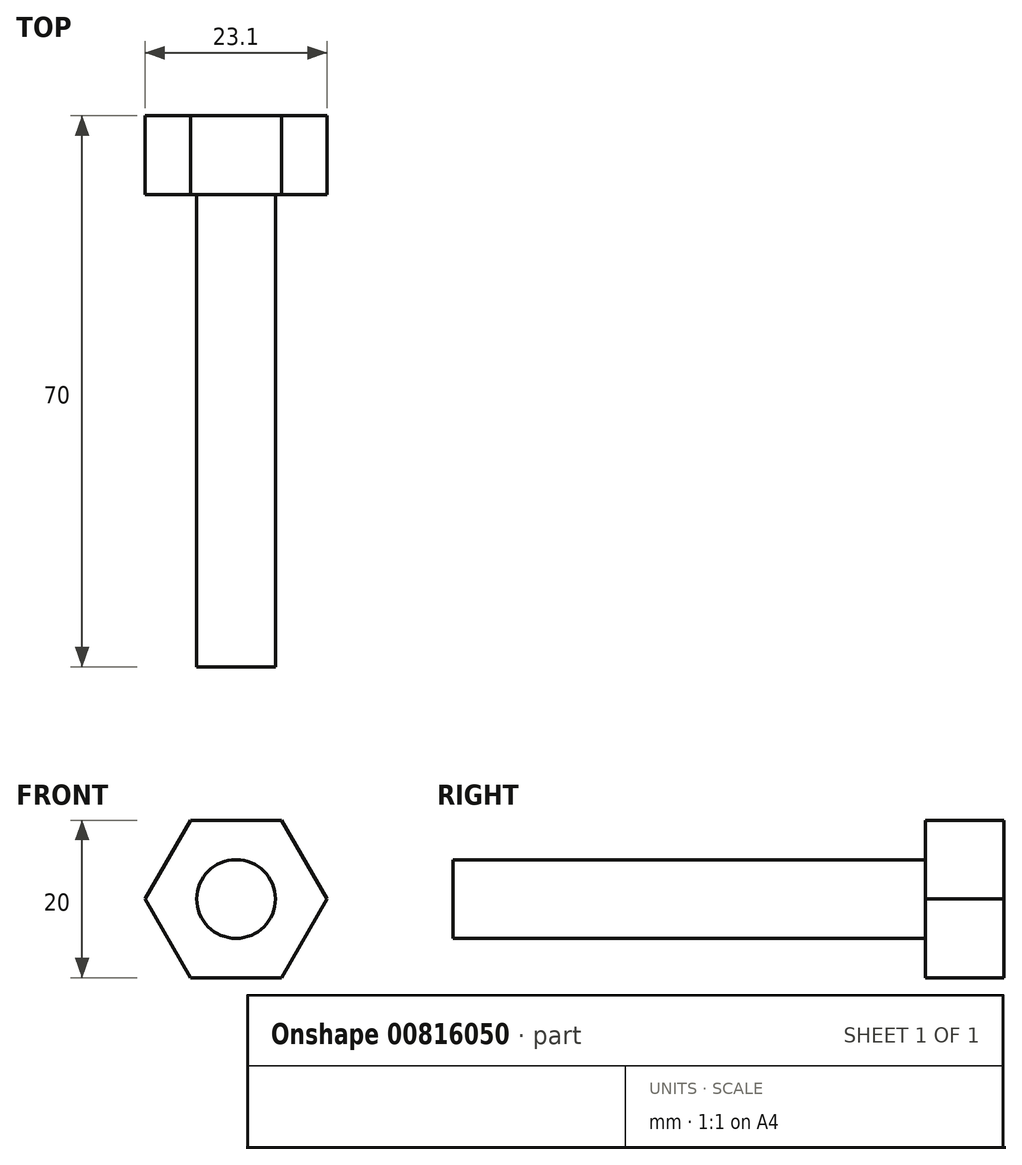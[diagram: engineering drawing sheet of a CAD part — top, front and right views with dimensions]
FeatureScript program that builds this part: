
annotation { "Feature Type Name" : "Feature", "Feature Type Description" : "" }
export const myFeature = defineFeature(function(context is Context, id is Id, definition is map)
    precondition{}
    {
        {
            var Q0;
            Q0=qCreatedBy(makeId("Front.planeOp"),FACE);
            var sketch = newSketch(context, id + "F0", { "sketchPlane" : qUnion([Q0])});
            skCircle(sketch, "E0", {"center": v(0, 0) * mm, "radius": 5 * mm});
            skSolve(sketch);
        }
        {
            var Q0;
            Q0=makeQuery(id+"F0.imprint","IMPRINT",FACE,{"disambiguationData":[TD([[makeQuery(id+"F0.imprint","IMPRINT",EDGE,{"derivedFrom":sQuery(id+"F0.wireOp",EDGE,"E0")}),1.0]])]});
            extrude(context, id + "F1", {"entities" : qUnion([Q0]), "depth" : 60 * mm, "offsetDistance" : 25 * mm});
        }
        {
            var Q0;
            Q0=makeQuery(id+"F1.opExtrude","CAP_FACE",FACE,{"disambiguationData":[OSD([sQuery(id+"F0.wireOp",EDGE,"E0")])],"isStart":true});
            var sketch = newSketch(context, id + "F2", { "sketchPlane" : qUnion([Q0])});
            skCircle(sketch, "E1.cCircle", {"center": v(0, 0) * mm, "radius": 10 * mm, "construction": true});
            skLineSegment(sketch, "E1.0", {"start": v(11.55, 0) * mm, "end": v(5.77, -10) * mm});
            skLineSegment(sketch, "E1.1", {"start": v(5.77, -10) * mm, "end": v(-5.77, -10) * mm});
            skLineSegment(sketch, "E1.2", {"start": v(-5.77, -10) * mm, "end": v(-11.55, 0) * mm});
            skLineSegment(sketch, "E1.3", {"start": v(-11.55, 0) * mm, "end": v(-5.77, 10) * mm});
            skLineSegment(sketch, "E1.4", {"start": v(-5.77, 10) * mm, "end": v(5.77, 10) * mm});
            skLineSegment(sketch, "E1.5", {"start": v(5.77, 10) * mm, "end": v(11.55, 0) * mm});
            skPoint(sketch, "E1.0.midPoint", {"position": v(8.66, -5) * mm});
            skSolve(sketch);
        }
        {
            var Q0;
            Q0=makeQuery(id+"F2.imprint","IMPRINT",FACE,{"disambiguationData":[TD([[makeQuery(id+"F2.imprint","IMPRINT",EDGE,{"derivedFrom":sQuery(id+"F2.wireOp",EDGE,"E1.0")}),-1.0]])]});
            var Q1;
            Q1=makeQuery(id+"F2.imprint","IMPRINT",FACE,{"disambiguationData":[TD([[makeQuery(id+"F2.imprint","IMPRINT",EDGE,{"derivedFrom":makeQuery(id+"F1.opExtrude","CAP_EDGE",EDGE,{"disambiguationData":[OSD([sQuery(id+"F0.wireOp",EDGE,"E0")])],"isStart":true})}),-1.0]])]});
            extrude(context, id + "F3", {"entities" : qUnion([Q0, Q1]), "operationType" : NewBodyOperationType.ADD, "depth" : 10 * mm, "offsetDistance" : 25 * mm});
        }
    });
